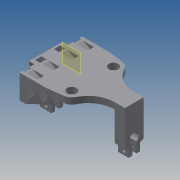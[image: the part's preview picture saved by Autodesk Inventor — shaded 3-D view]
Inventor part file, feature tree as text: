
AUTODESK INVENTOR PART (.ipt)
format: ipt  version: 2014 (Build 180170000, 170)  size: 483,328 bytes
history: native  units: in
note: dims shown in document units (in); Inventor stores cm internally (conversion verified against a paired STEP export)
features: extrude x15, fillet x15, sketch x15, mirror x2, plane x1
ambient origin geometry x8: Origin, YZ Plane, XZ Plane, XY Plane, X Axis, Y Axis, Z Axis, Center Point
bodies: Solid1 (feature_tree)
feature tree (48):
  extrude  "Extrusion1"  Depth=1.0441in
  extrude  "Extrusion11"  Depth=0.3543in
  extrude  "Extrusion12"  Depth=2.3622in
  extrude  "Extrusion13"  Depth=0.9843in
  mirror  "Mirror1"
  extrude  "Extrusion14"  Depth=0.2362in
  extrude  "Extrusion4"  Depth=0.6299in
  extrude  "Extrusion15"  Depth=0.1181in
  extrude  "Extrusion16"  Depth=0.3543in
  extrude  "Extrusion17"  Depth=0.3937in
  extrude  "Extrusion18"  Depth=0.7087in
  extrude  "Extrusion19"  Depth=0.3937in
  extrude  "Extrusion20"  Depth=0.7087in
  extrude  "Extrusion21"  Depth=0.1181in TaperAngle=0.0deg
  extrude  "Extrusion22"  Depth=0.1575in TaperAngle=0.0deg
  plane  "Work Plane1"
  extrude  "Extrusion24"  Depth=0.2362in
  mirror  "Mirror2"
  fillet  "Fillet8"  Radius=0.1575in
  fillet  "Fillet9"  Radius=4.0187in
  fillet  "Fillet10"  Radius=0.3937in
  fillet  "Fillet11"  Radius=0.315in
  fillet  "Fillet12"  Radius=0.5512in
  fillet  "Fillet13"  Radius=0.1181in
  fillet  "Fillet14"  Radius=0.7874in
  fillet  "Fillet15"  Radius=0.1969in
  fillet  "Fillet16"  Radius=0.1575in
  fillet  "Fillet17"  Radius=4.0719in
  fillet  "Fillet18"  Radius=0.1378in
  fillet  "Fillet19"  Radius=0.3937in
  fillet  "Fillet20"  Radius=4.0719in
  fillet  "Fillet21"  Radius=4.0719in
  fillet  "Fillet22"  Radius=0.1319in
  sketch  "Sketch1"  dims[d0=1.1713in d1=1.0441in]
  sketch  "Sketch2"  dims[d2=1.5748in d3=0.3543in]
  sketch  "Sketch3"  dims[d4=0.6299in d5=2.3622in]
  sketch  "Sketch4"  dims[d6=0.5906in d7=0.9843in]
  sketch  "Sketch5"  dims[d9=0.2362in d10=0.0in d11=0.2362in]
  sketch  "Sketch6"  dims[d12=1.5748in d13=0.6299in]
  sketch  "Sketch11"  dims[d15=0.3346in d16=0.1181in]
  sketch  "Sketch13"  dims[d26=2.5123in d27=0.0in d28=0.3543in]
  sketch  "Sketch14"  dims[d35=1.2598in d66=0.3937in]
  sketch  "Sketch15"  dims[d67=0.7087in d68=1.5748in]
  sketch  "Sketch16"  dims[d69=2.3622in d70=0.0in d71=0.3937in]
  sketch  "Sketch17"  dims[d72=0.7087in d73=0.0in d74=0.0591in]
  sketch  "Sketch18"  dims[d75=0.315in d76=0.1181in d77=0.0in]
  sketch  "Sketch19"  dims[d78=0.0394in d79=0.1575in d80=0.0in]
  sketch  "Sketch21"  dims[d81=0.9055in d82=0.2362in d83=0.1575in d84=4.0187in d85=0.0in d87=0.3937in d88=0.315in d89=0.5512in d90=0.1181in d91=0.0in d92=0.7874in d93=0.1969in d94=0.0in d95=0.1575in d96=4.0719in d97=0.0in d98=0.1378in d99=0.3937in d100=4.0719in d101=0.0in d104=4.0719in d105=0.0in d106=0.1319in d107=0.1969in d108=4.0719in d109=0.0in d111=0.1181in d112=0.1969in d113=0.1181in d114=0.2362in d115=0.0in d117=0.1575in d119=0.1969in d123=0.1181in d124=0.2362in d125=0.0in d126=0.1181in d127=0.0787in d128=0.0984in d129=0.0394in d130=0.0394in d131=0.0197in d132=0.0197in d133=0.0197in d134=0.0197in d135=0.0197in d136=0.0197in d137=0.0197in d138=0.0197in d139=0.0197in d140=0.0295in d141=0.0295in d142=0.0295in]
